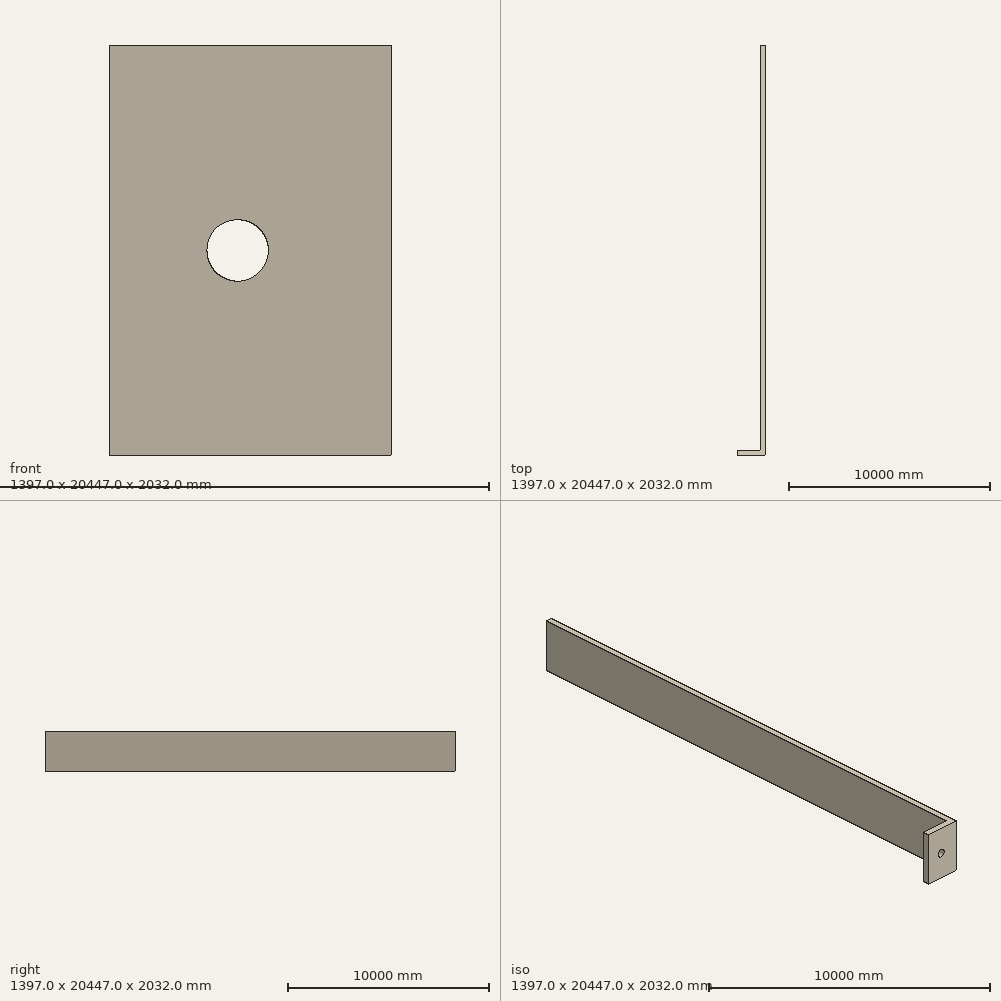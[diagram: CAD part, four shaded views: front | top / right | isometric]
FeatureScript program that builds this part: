
annotation { "Feature Type Name" : "Feature", "Feature Type Description" : "" }
export const myFeature = defineFeature(function(context is Context, id is Id, definition is map)
    precondition{}
    {
        {
            var Q0;
            Q0=qCreatedBy(makeId("Right.planeOp"),FACE);
            var sketch = newSketch(context, id + "F0", { "sketchPlane" : qUnion([Q0])});
            skLineSegment(sketch, "E0.bottom", {"start": v(127, 1016) * mm, "end": v(-127, 1016) * mm});
            skLineSegment(sketch, "E0.top", {"start": v(127, -1016) * mm, "end": v(-127, -1016) * mm});
            skLineSegment(sketch, "E0.left", {"start": v(127, 1016) * mm, "end": v(127, -1016) * mm});
            skLineSegment(sketch, "E0.right", {"start": v(-127, 1016) * mm, "end": v(-127, -1016) * mm});
            skSolve(sketch);
        }
        {
            var Q0;
            Q0=qCreatedBy(makeId("Top.planeOp"),FACE);
            var sketch = newSketch(context, id + "F1", { "sketchPlane" : qUnion([Q0])});
            skLineSegment(sketch, "E1", {"start": v(0, 0) * mm, "end": v(1270, 0) * mm});
            skLineSegment(sketch, "E2", {"start": v(1270, 0) * mm, "end": v(1270, 20320) * mm});
            skSolve(sketch);
        }
        {
            var Q0;
            Q0=makeQuery(id+"F0.imprint","IMPRINT",FACE,{"disambiguationData":[TD([[makeQuery(id+"F0.imprint","IMPRINT",EDGE,{"derivedFrom":sQuery(id+"F0.wireOp",EDGE,"E0.bottom")}),1.0]])]});
            var Q1;
            Q1 = qConstructionFilter(qBodyType(qCreatedBy(id + "F1" ,EDGE), BodyType.WIRE), ConstructionObject.NO);
            sweep(context, id + "F2", {"profiles" : qUnion([Q0]), "path" : qUnion([Q1])});
        }
        {
            var Q0;
            Q0=makeQuery(id+"F2.opSweep","SWEPT_FACE",FACE,{"disambiguationData":[OSD([sQuery(id+"F0.wireOp",EDGE,"E0.right"),sQuery(id+"F1.wireOp",EDGE,"E1")])]});
            var sketch = newSketch(context, id + "F3", { "sketchPlane" : qUnion([Q0])});
            skLineSegment(sketch, "E3", {"start": v(-442.83, 0) * mm, "end": v(1712.83, 0) * mm, "construction": true});
            skPoint(sketch, "E3.startSnap0", {"position": v(0, 0) * mm});
            skPoint(sketch, "E3.endSnap0", {"position": v(1397, 0) * mm});
            skPoint(sketch, "E4", {"position": v(635, 0) * mm});
            skSolve(sketch);
        }
        {
            var Q0;
            Q0=sQuery(id+"F3.wireOp",VERTEX,"E4");
            var Q1;
            Q1=makeQuery(id+"F2.opSweep","SWEPT_BODY",BODY,{"disambiguationData":[OSD([sQuery(id+"F0.wireOp",EDGE,"E0.bottom"),sQuery(id+"F0.wireOp",EDGE,"E0.top"),sQuery(id+"F0.wireOp",EDGE,"E0.left"),sQuery(id+"F0.wireOp",EDGE,"E0.right"),sQuery(id+"F1.wireOp",EDGE,"E2")])]});
            hole(context, id + "F4", {"style" : HoleStyle.SIMPLE, "endStyle" : HoleEndStyle.BLIND, "holeDiameter" : 304.8 * mm, "holeDepth" : 254 * mm, "isTappedThrough" : true, "tappedDepth" : 12.7 * mm, "tapClearance" : 3, "locations" : qUnion([Q0]), "scope" : qUnion([Q1])});
        }
    });
